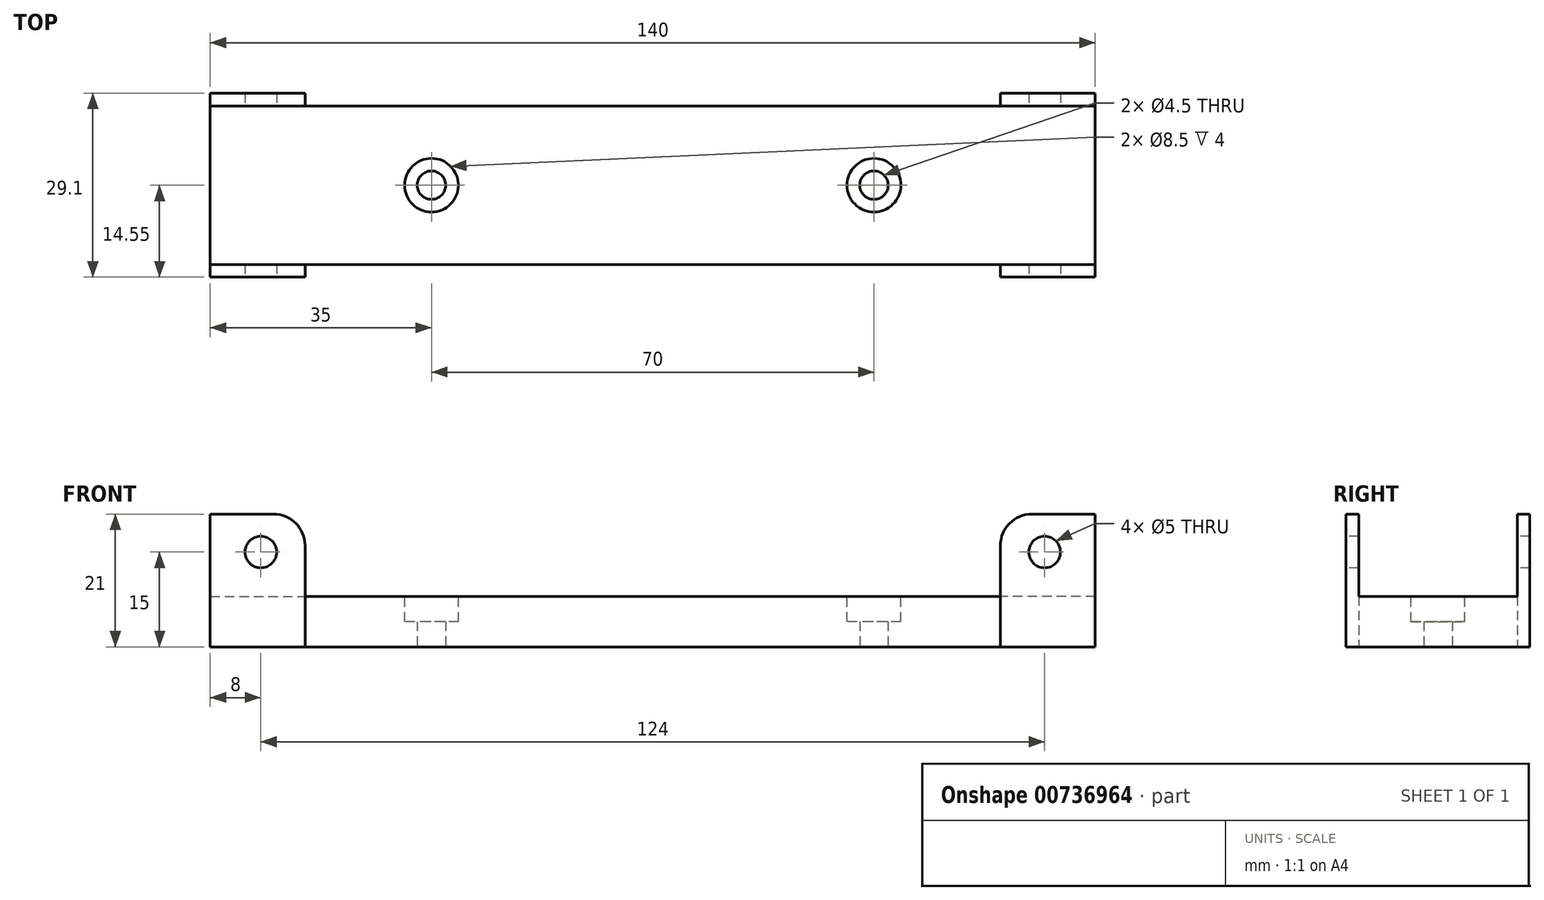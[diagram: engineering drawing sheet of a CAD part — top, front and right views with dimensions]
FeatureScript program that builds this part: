
annotation { "Feature Type Name" : "Feature", "Feature Type Description" : "" }
export const myFeature = defineFeature(function(context is Context, id is Id, definition is map)
    precondition{}
    {
        {
            var Q0;
            Q0=qCreatedBy(makeId("Top.planeOp"),FACE);
            var sketch = newSketch(context, id + "F0", { "sketchPlane" : qUnion([Q0])});
            skLineSegment(sketch, "E0.bottom", {"start": v(70, -12.55) * mm, "end": v(-70, -12.55) * mm});
            skLineSegment(sketch, "E0.left", {"start": v(70, -12.55) * mm, "end": v(70, 12.55) * mm});
            skLineSegment(sketch, "E0.right", {"start": v(-70, -12.55) * mm, "end": v(-70, 12.55) * mm});
            skPoint(sketch, "E0.middle", {"position": v(0, 0) * mm});
            skLineSegment(sketch, "E1.bottom", {"start": v(-70, -12.55) * mm, "end": v(-55, -12.55) * mm});
            skLineSegment(sketch, "E1.top", {"start": v(-70, -14.55) * mm, "end": v(-55, -14.55) * mm});
            skLineSegment(sketch, "E1.left", {"start": v(-70, -12.55) * mm, "end": v(-70, -14.55) * mm});
            skLineSegment(sketch, "E1.right", {"start": v(-55, -12.55) * mm, "end": v(-55, -14.55) * mm});
            skLineSegment(sketch, "E2.bottom", {"start": v(70, -12.55) * mm, "end": v(55, -12.55) * mm});
            skLineSegment(sketch, "E2.top", {"start": v(70, -14.55) * mm, "end": v(55, -14.55) * mm});
            skLineSegment(sketch, "E2.left", {"start": v(70, -12.55) * mm, "end": v(70, -14.55) * mm});
            skLineSegment(sketch, "E2.right", {"start": v(55, -12.55) * mm, "end": v(55, -14.55) * mm});
            skPoint(sketch, "E3", {"position": v(0, 12.55) * mm});
            skPoint(sketch, "E4.center.orphan", {"position": v(0, 20) * mm});
            skPoint(sketch, "E5.orphan", {"position": v(7.5, 12.55) * mm});
            skPoint(sketch, "E6.bottom.start.orphan", {"position": v(-7.5, 12.55) * mm});
            skLineSegment(sketch, "E7", {"start": v(-70, 12.55) * mm, "end": v(70, 12.55) * mm});
            skCircle(sketch, "E8", {"center": v(-35, 0) * mm, "radius": 2.25 * mm});
            skCircle(sketch, "E9", {"center": v(-35, 0) * mm, "radius": 4.25 * mm});
            skCircle(sketch, "E10", {"center": v(35, 0) * mm, "radius": 2.25 * mm});
            skCircle(sketch, "E11", {"center": v(35, 0) * mm, "radius": 4.25 * mm});
            skLineSegment(sketch, "E12.bottom", {"start": v(-70, 12.55) * mm, "end": v(-55, 12.55) * mm});
            skLineSegment(sketch, "E12.top", {"start": v(-70, 14.55) * mm, "end": v(-55, 14.55) * mm});
            skLineSegment(sketch, "E12.left", {"start": v(-70, 12.55) * mm, "end": v(-70, 14.55) * mm});
            skLineSegment(sketch, "E12.right", {"start": v(-55, 12.55) * mm, "end": v(-55, 14.55) * mm});
            skLineSegment(sketch, "E13.bottom", {"start": v(70, 12.55) * mm, "end": v(55, 12.55) * mm});
            skLineSegment(sketch, "E13.top", {"start": v(70, 14.55) * mm, "end": v(55, 14.55) * mm});
            skLineSegment(sketch, "E13.left", {"start": v(70, 12.55) * mm, "end": v(70, 14.55) * mm});
            skLineSegment(sketch, "E13.right", {"start": v(55, 12.55) * mm, "end": v(55, 14.55) * mm});
            skSolve(sketch);
        }
        {
            var Q0;
            {var subQ0=sQuery(id+"F0.wireOp",EDGE,"E0.left");Q0=makeQuery(id+"F0.imprint","IMPRINT",FACE,{"disambiguationData":[TD([[makeQuery(id+"F0.imprint","IMPRINT",EDGE,{"derivedFrom":subQ0}),1.0]])]});}
            var Q1;
            Q1=makeQuery(id+"F0.imprint","IMPRINT",FACE,{"disambiguationData":[TD([[makeQuery(id+"F0.imprint","IMPRINT",EDGE,{"derivedFrom":sQuery(id+"F0.wireOp",EDGE,"E6.bottom")}),1.0]])]});
            var Q2;
            Q2=makeQuery(id+"F0.imprint","IMPRINT",FACE,{"disambiguationData":[TD([[makeQuery(id+"F0.imprint","IMPRINT",EDGE,{"derivedFrom":sQuery(id+"F0.wireOp",EDGE,"E8")}),-1.0]])]});
            var Q3;
            Q3=makeQuery(id+"F0.imprint","IMPRINT",FACE,{"disambiguationData":[TD([[makeQuery(id+"F0.imprint","IMPRINT",EDGE,{"derivedFrom":sQuery(id+"F0.wireOp",EDGE,"E10")}),-1.0]])]});
            extrude(context, id + "F1", {"entities" : qUnion([Q0, Q1, Q2, Q3]), "depth" : 8 * mm, "offsetDistance" : 25 * mm});
        }
        {
            var Q0;
            Q0=makeQuery(id+"F0.imprint","IMPRINT",FACE,{"disambiguationData":[TD([[makeQuery(id+"F0.imprint","IMPRINT",EDGE,{"derivedFrom":sQuery(id+"F0.wireOp",EDGE,"E1.top")}),1.0]])]});
            var Q1;
            Q1=makeQuery(id+"F0.imprint","IMPRINT",FACE,{"disambiguationData":[TD([[makeQuery(id+"F0.imprint","IMPRINT",EDGE,{"derivedFrom":sQuery(id+"F0.wireOp",EDGE,"E2.top")}),-1.0]])]});
            var Q2;
            Q2=makeQuery(id+"F0.imprint","IMPRINT",FACE,{"disambiguationData":[TD([[makeQuery(id+"F0.imprint","IMPRINT",EDGE,{"derivedFrom":sQuery(id+"F0.wireOp",EDGE,"E12.top")}),-1.0]])]});
            var Q3;
            Q3=makeQuery(id+"F0.imprint","IMPRINT",FACE,{"disambiguationData":[TD([[makeQuery(id+"F0.imprint","IMPRINT",EDGE,{"derivedFrom":sQuery(id+"F0.wireOp",EDGE,"E13.top")}),1.0]])]});
            extrude(context, id + "F2", {"entities" : qUnion([Q0, Q1, Q2, Q3]), "operationType" : NewBodyOperationType.ADD, "depth" : 21 * mm, "offsetDistance" : 25 * mm});
        }
        {
            var Q0;
            Q0=makeQuery(id+"F2.opExtrude","SWEPT_FACE",FACE,{"disambiguationData":[OSD([sQuery(id+"F0.wireOp",EDGE,"E1.top")])]});
            var sketch = newSketch(context, id + "F3", { "sketchPlane" : qUnion([Q0])});
            skCircle(sketch, "E14", {"center": v(-62, 15) * mm, "radius": 2.5 * mm});
            skCircle(sketch, "E15", {"center": v(62, 15) * mm, "radius": 2.5 * mm});
            skLineSegment(sketch, "E16.0", {"start": v(-55, 8) * mm, "end": v(55, 8) * mm});
            skSolve(sketch);
        }
        {
            var Q0;
            Q0=makeQuery(id+"F3.imprint","IMPRINT",FACE,{"disambiguationData":[TD([[makeQuery(id+"F3.imprint","IMPRINT",EDGE,{"derivedFrom":sQuery(id+"F3.wireOp",EDGE,"E14")}),1.0]])]});
            var Q1;
            Q1=makeQuery(id+"F3.imprint","IMPRINT",FACE,{"disambiguationData":[TD([[makeQuery(id+"F3.imprint","IMPRINT",EDGE,{"derivedFrom":sQuery(id+"F3.wireOp",EDGE,"E15")}),1.0]])]});
            extrude(context, id + "F4", {"entities" : qUnion([Q0, Q1]), "operationType" : NewBodyOperationType.REMOVE, "endBound" : BoundingType.THROUGH_ALL, "oppositeDirection" : true, "depth" : 25 * mm, "offsetDistance" : 25 * mm});
        }
        {
            var Q0;
            Q0=makeQuery(id+"F2.opExtrude","CAP_EDGE",EDGE,{"disambiguationData":[OSD([sQuery(id+"F0.wireOp",EDGE,"E1.right")])],"isStart":false});
            var Q1;
            Q1=makeQuery(id+"F2.opExtrude","CAP_EDGE",EDGE,{"disambiguationData":[OSD([sQuery(id+"F0.wireOp",EDGE,"E2.right")])],"isStart":false});
            var Q2;
            Q2=makeQuery(id+"F2.opExtrude","CAP_EDGE",EDGE,{"disambiguationData":[OSD([sQuery(id+"F0.wireOp",EDGE,"E12.right")])],"isStart":false});
            var Q3;
            Q3=makeQuery(id+"F2.opExtrude","CAP_EDGE",EDGE,{"disambiguationData":[OSD([sQuery(id+"F0.wireOp",EDGE,"E13.right")])],"isStart":false});
            fillet(context, id + "F5", {"entities" : qUnion([Q0, Q1, Q2, Q3]), "radius" : 5 * mm, "tangentPropagation" : true, "allowEdgeOverflow" : false});
        }
        {
            var Q0;
            Q0=makeQuery(id+"F1.opExtrude","CAP_FACE",FACE,{"disambiguationData":[OSD([sQuery(id+"F0.wireOp",EDGE,"E0.bottom"),sQuery(id+"F0.wireOp",EDGE,"E0.left"),sQuery(id+"F0.wireOp",EDGE,"E0.right"),sQuery(id+"F0.wireOp",EDGE,"E7"),sQuery(id+"F0.wireOp",EDGE,"E8"),sQuery(id+"F0.wireOp",EDGE,"E10")])],"isStart":false});
            var sketch = newSketch(context, id + "F6", { "sketchPlane" : qUnion([Q0])});
            skCircle(sketch, "E17.0", {"center": v(-35, 0) * mm, "radius": 4.25 * mm});
            skCircle(sketch, "E17.1", {"center": v(35, 0) * mm, "radius": 4.25 * mm});
            skSolve(sketch);
        }
        {
            var Q0;
            Q0 = qSketchRegion(id + "F6", true);
            extrude(context, id + "F7", {"entities" : qUnion([Q0]), "operationType" : NewBodyOperationType.REMOVE, "oppositeDirection" : true, "depth" : 4 * mm, "offsetDistance" : 25 * mm});
        }
    });
